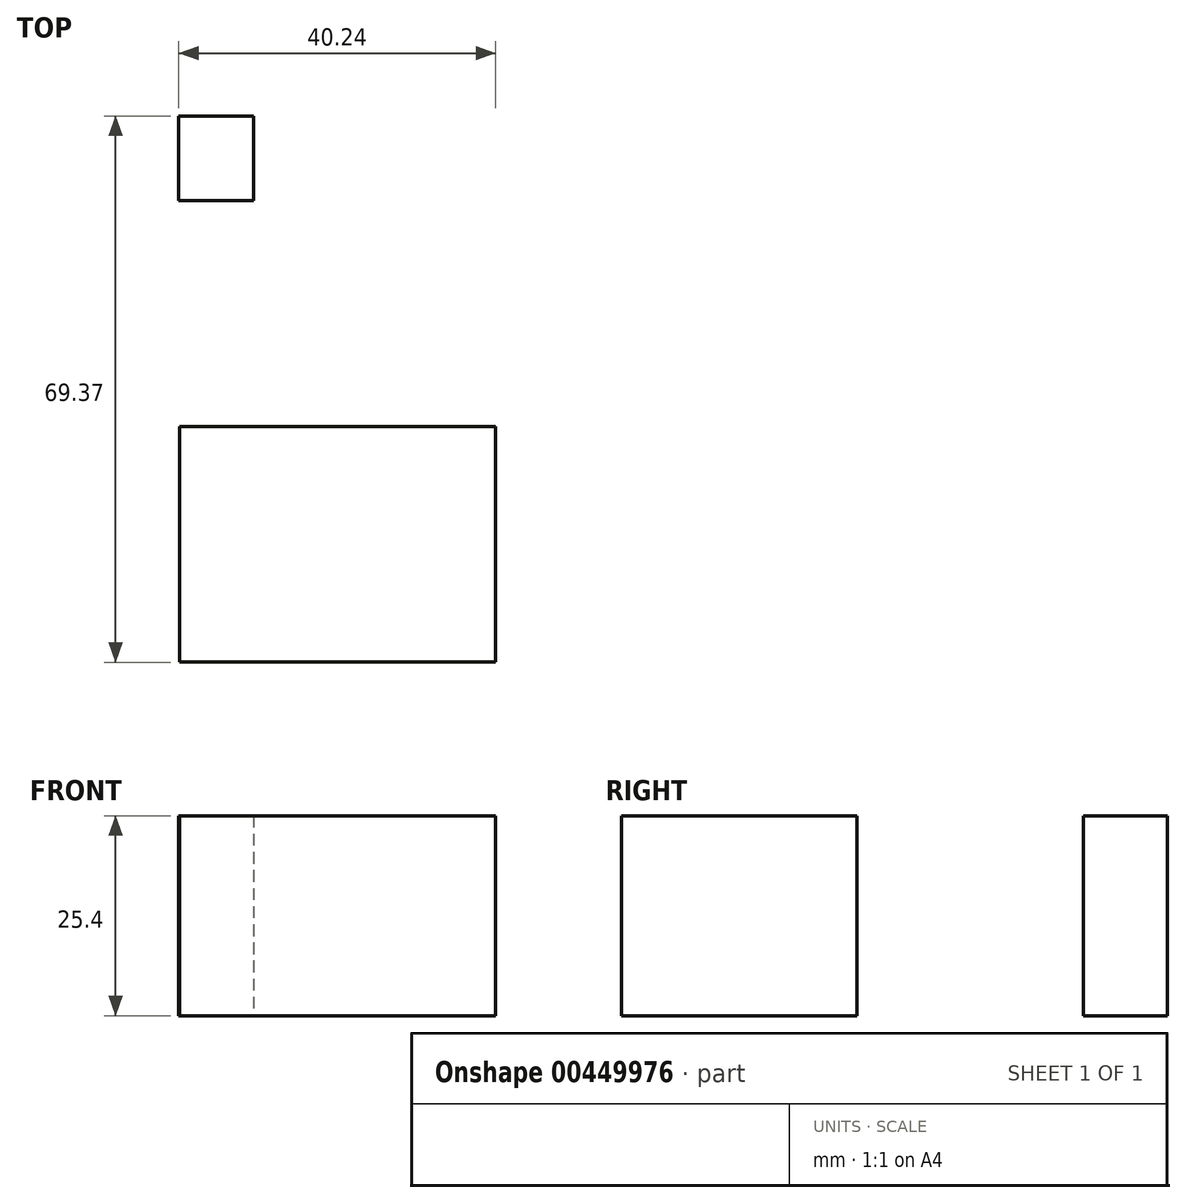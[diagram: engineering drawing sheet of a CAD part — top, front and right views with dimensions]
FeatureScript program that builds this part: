
annotation { "Feature Type Name" : "Feature", "Feature Type Description" : "" }
export const myFeature = defineFeature(function(context is Context, id is Id, definition is map)
    precondition{}
    {
        {
            var Q0;
            Q0=qCreatedBy(makeId("Top.planeOp"),FACE);
            var sketch = newSketch(context, id + "F0", { "sketchPlane" : qUnion([Q0])});
            skLineSegment(sketch, "E0.bottom", {"start": v(-107.69, 23.95) * mm, "end": v(-98.2, 23.95) * mm});
            skLineSegment(sketch, "E0.top", {"start": v(-107.69, 13.25) * mm, "end": v(-98.2, 13.25) * mm});
            skLineSegment(sketch, "E0.left", {"start": v(-107.69, 23.95) * mm, "end": v(-107.69, 13.25) * mm});
            skLineSegment(sketch, "E0.right", {"start": v(-98.2, 23.95) * mm, "end": v(-98.2, 13.25) * mm});
            skLineSegment(sketch, "E1.bottom", {"start": v(-107.55, -15.47) * mm, "end": v(-67.45, -15.47) * mm});
            skLineSegment(sketch, "E1.top", {"start": v(-107.55, -45.42) * mm, "end": v(-67.45, -45.42) * mm});
            skLineSegment(sketch, "E1.left", {"start": v(-107.55, -15.47) * mm, "end": v(-107.55, -45.42) * mm});
            skLineSegment(sketch, "E1.right", {"start": v(-67.45, -15.47) * mm, "end": v(-67.45, -45.42) * mm});
            skSolve(sketch);
        }
        {
            var Q0;
            Q0 = qSketchRegion(id + "F0", true);
            extrude(context, id + "F1", {"entities" : qUnion([Q0]), "depth" : 25.4 * mm});
        }
    });
